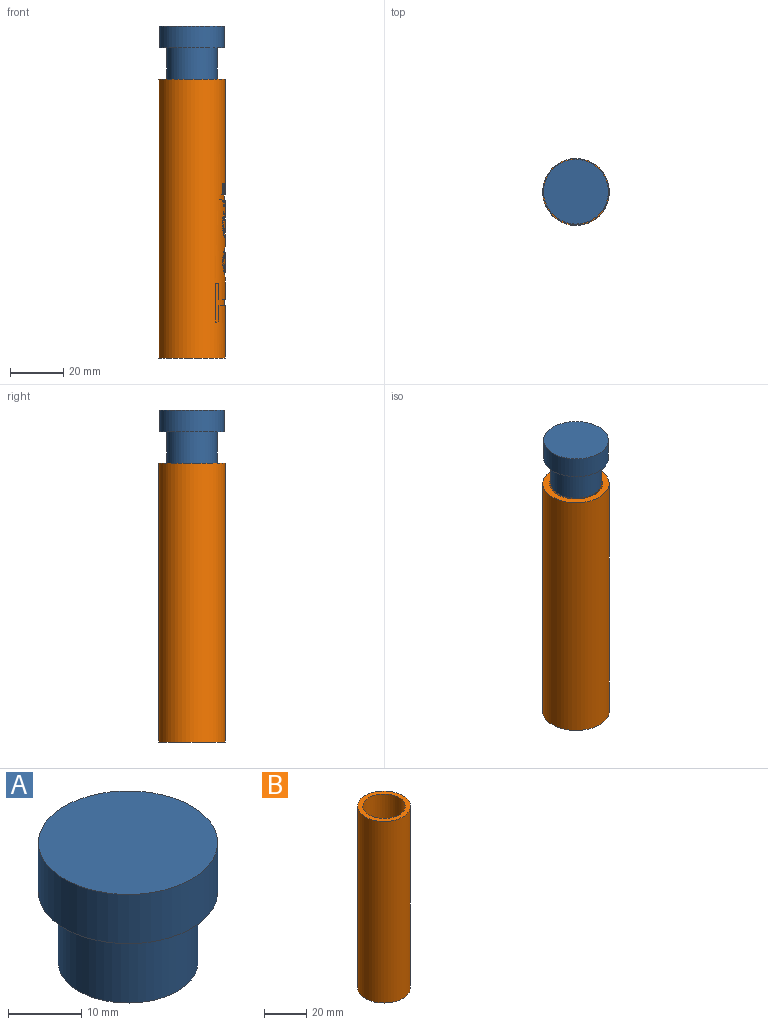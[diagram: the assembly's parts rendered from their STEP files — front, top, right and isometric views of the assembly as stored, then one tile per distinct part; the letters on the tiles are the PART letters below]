
ASSEMBLY  parts=2 mates=1
PART A: 7 faces, bbox 24.4x24.4x20 mm
  f0: cylinder r=9.5mm len=19mm, axis (0,0,-1), area 704.3mm2, adj f1,f5
  f1: plane 19x19mm, normal (0,0,-1), area 129.6mm2, adj f0,f2
  f2: cylinder r=7mm len=17.5mm, axis (0,0,-1), area 769.7mm2, adj f1,f3
  f3: plane 14x14mm, normal (0,0,-1), area 153.9mm2, adj f2
  f4: cylinder r=12.2mm len=24.4mm, axis (0,0,1), area 628.6mm2, adj f5,f6
  f5: plane 24.4x24.4mm, normal (0,0,-1), area 184.1mm2, adj f0,f4
  f6: plane 24.4x24.4mm, normal (0,0,1), area 467.6mm2, adj f4
PART B: 81 faces, bbox 25x25x105 mm
  f0: cylinder r=12.5mm len=105mm, axis (0,0,-1), area 7945.9mm2, adj f1,f2,f9,f10,f11,f12,f13,f14
  f1: plane 25x25mm, normal (0,0,1), area 176.7mm2, adj f0,f4
  f2: plane 25x25mm, normal (0,0,-1), area 490.9mm2, adj f0
  f3: cone r=0mm half-angle=59deg, axis (0,0,1), area 366.5mm2, adj f4
  f4: cylinder r=10mm len=95mm, axis (0,0,1), area 5969mm2, adj f1,f3
  f5: bspline ~3.19x0.93mm, area 1.3mm2, adj f6,f23,f24,f25
  f6: plane 7.63x0.4mm, normal (-0.07,1,0), area 3.1mm2, adj f5,f7,f24,f25
  f7: bspline ~3.16x1.23mm, area 1.4mm2, adj f6,f8,f24,f25
  f8: bspline ~2.8x1.19mm, area 1.2mm2, adj f7,f23,f24,f25
  f9: bspline ~2.22x0.8mm, area 0.9mm2, adj f0,f10,f22,f24
  f10: plane 1.8x1.47mm, normal (0,0,-1), area 0.8mm2, adj f0,f9,f11,f24
  f11: bspline ~4.66x1.03mm, area 1.9mm2, adj f0,f10,f12,f24
  f12: bspline ~3.47x1.31mm, area 1.5mm2, adj f0,f11,f13,f24
  f13: bspline ~3.71x1.76mm, area 1.7mm2, adj f0,f12,f14,f24
  f14: plane 10.05x0.39mm, normal (0.21,-0.98,0), area 4mm2, adj f0,f13,f15,f24
  f15: plane 1.42x0.61mm, normal (0,0,-1), area 0.6mm2, adj f0,f14,f16,f24
  f16: bspline ~4.72x1.6mm, area 2mm2, adj f0,f15,f17,f24
  f17: bspline ~4.34x1.8mm, area 1.9mm2, adj f0,f16,f18,f24
  f18: bspline ~4.67x2.06mm, area 2.1mm2, adj f0,f17,f19,f24
  f19: bspline ~5.56x1.74mm, area 2.4mm2, adj f0,f18,f20,f24
  f20: bspline ~5.05x2.5mm, area 2.3mm2, adj f0,f19,f21,f24
  f21: bspline ~5.11x1.73mm, area 2.2mm2, adj f0,f20,f22,f24
  f22: bspline ~2.52x0.44mm, area 1mm2, adj f0,f9,f21,f24
  f23: bspline ~2.67x1.16mm, area 1.2mm2, adj f5,f8,f24,f25
  f24: cylinder r=12.1mm len=13.54mm, axis (0,0,-1), area 87.3mm2, adj f5,f6,f7,f8,f9,f10,f11,f12
  f25: cylinder r=12.5mm len=7.63mm, axis (0,0,-1), area 23.9mm2, adj f5,f6,f7,f8,f23
  f26: bspline ~1.93x1.31mm, area 0.9mm2, adj f0,f27,f44,f45
  f27: plane 8.4x1.48mm, normal (0,0,-1), area 3.4mm2, adj f0,f26,f28,f45
  f28: plane 4.24x0.39mm, normal (-0.26,-0.97,0), area 1.7mm2, adj f0,f27,f29,f45
  f29: plane 1.73x0.93mm, normal (0,0,-1), area 0.7mm2, adj f0,f28,f30,f45
  f30: plane 4.24x0.37mm, normal (0.39,0.92,0), area 1.7mm2, adj f0,f29,f31,f45
  f31: plane 3.06x2.03mm, normal (0,0,-1), area 1.3mm2, adj f0,f30,f32,f45
  f32: plane 1.28x0.31mm, normal (0.62,0.78,0), area 0.5mm2, adj f0,f31,f33,f45
  f33: bspline ~2.82x1.93mm, area 1.3mm2, adj f0,f32,f34,f45
  f34: bspline ~2.09x0.99mm, area 0.9mm2, adj f0,f33,f35,f45
  f35: plane 1.12x0.7mm, normal (0,0,1), area 0.4mm2, adj f0,f34,f36,f45
  f36: plane 2.09x0.39mm, normal (-0.26,-0.97,0), area 0.8mm2, adj f0,f35,f37,f45
  f37: plane 8.48x1.52mm, normal (0,0,1), area 3.4mm2, adj f0,f36,f38,f45
  f38: bspline ~4.23x3.8mm, area 2.8mm2, adj f0,f37,f39,f45
  f39: bspline ~1.26x0.36mm, area 0.5mm2, adj f0,f38,f40,f45
  f40: bspline ~1.06x0.48mm, area 0.4mm2, adj f0,f39,f41,f45
  f41: plane 1.54x1.37mm, normal (0,0,-1), area 0.7mm2, adj f0,f40,f42,f45
  f42: bspline ~0.87x0.43mm, area 0.4mm2, adj f0,f41,f43,f45
  f43: bspline ~1.13x0.37mm, area 0.5mm2, adj f0,f42,f44,f45
  f44: bspline ~1.72x0.8mm, area 0.8mm2, adj f0,f26,f43,f45
  f45: cylinder r=12.1mm len=16.11mm, axis (0,0,-1), area 53.9mm2, adj f26,f27,f28,f29,f30,f31,f32,f33
  f46: bspline ~3.51x1.91mm, area 1.6mm2, adj f0,f47,f70,f71
  f47: bspline ~2.56x1.09mm, area 1.1mm2, adj f0,f46,f48,f71
  f48: bspline ~0.97x0.78mm, area 0.5mm2, adj f0,f47,f49,f71
  f49: bspline ~1.01x0.48mm, area 0.4mm2, adj f0,f48,f50,f71
  f50: bspline ~1.39x0.8mm, area 0.7mm2, adj f0,f49,f51,f71
  f51: bspline ~2.37x0.57mm, area 1mm2, adj f0,f50,f52,f71
  f52: bspline ~3.98x0.96mm, area 1.6mm2, adj f0,f51,f53,f71
  f53: bspline ~1.81x0.86mm, area 0.8mm2, adj f0,f52,f54,f71
  f54: bspline ~4.61x1.02mm, area 1.9mm2, adj f0,f53,f55,f71
  f55: bspline ~3.98x1.09mm, area 1.7mm2, adj f0,f54,f56,f71
  f56: bspline ~2.79x1.45mm, area 1.3mm2, adj f0,f55,f57,f71
  f57: bspline ~1.71x0.49mm, area 0.7mm2, adj f0,f56,f58,f71
  f58: bspline ~1.29x1.28mm, area 0.7mm2, adj f0,f57,f59,f71
  f59: bspline ~2.9x1.35mm, area 1.3mm2, adj f0,f58,f60,f71
  f60: bspline ~2.89x1.46mm, area 1.3mm2, adj f0,f59,f61,f71
  f61: bspline ~1.47x0.93mm, area 0.7mm2, adj f0,f60,f62,f71
  f62: bspline ~1.63x1.18mm, area 0.8mm2, adj f0,f61,f63,f71
  f63: bspline ~2.66x0.67mm, area 1.1mm2, adj f0,f62,f64,f71
  f64: bspline ~2.33x0.5mm, area 0.9mm2, adj f0,f63,f65,f71
  f65: bspline ~2.26x0.91mm, area 1mm2, adj f0,f64,f66,f71
  f66: plane 1.86x1.52mm, normal (0,0,1), area 0.8mm2, adj f0,f65,f67,f71
  f67: bspline ~4.53x0.93mm, area 1.9mm2, adj f0,f66,f68,f71
  f68: bspline ~4.26x1.07mm, area 1.8mm2, adj f0,f67,f69,f71
  f69: bspline ~2.8x2.01mm, area 1.4mm2, adj f0,f68,f70,f71
  f70: bspline ~2.36x1.19mm, area 1mm2, adj f0,f46,f69,f71
  f71: cylinder r=12.1mm len=13.54mm, axis (0,0,-1), area 60.2mm2, adj f46,f47,f48,f49,f50,f51,f52,f53
  f72: plane 6.17x0.32mm, normal (-0.59,-0.81,0), area 2.5mm2, adj f0,f73,f79,f80
  f73: plane 1.76x1.59mm, normal (0,0,-1), area 0.8mm2, adj f0,f72,f74,f80
  f74: plane 14.6x0.28mm, normal (0.71,0.7,0), area 5.8mm2, adj f0,f73,f75,f80
  f75: plane 1.76x1.59mm, normal (0,0,1), area 0.8mm2, adj f0,f74,f76,f80
  f76: plane 6.17x0.32mm, normal (-0.59,-0.81,0), area 2.5mm2, adj f0,f75,f77,f80
  f77: plane 16.04x3.8mm, normal (0,0,1), area 6.9mm2, adj f0,f76,f78,f80
  f78: plane 2.26x0.29mm, normal (0.69,-0.72,0), area 0.9mm2, adj f0,f77,f79,f80
  f79: plane 16.04x3.8mm, normal (0,0,-1), area 6.9mm2, adj f0,f72,f78,f80
  f80: cylinder r=12.1mm len=17mm, axis (0,0,-1), area 66.7mm2, adj f72,f73,f74,f75,f76,f77,f78,f79
PLACE A t=(-22.17,-0.81,-34.52)mm
PLACE B t=(-22.17,-0.81,-34.52)mm
MATE fastened A.f0 <-> B.f0  axis (0,0,-1) through (-22.17,-0.81,70.48)mm
